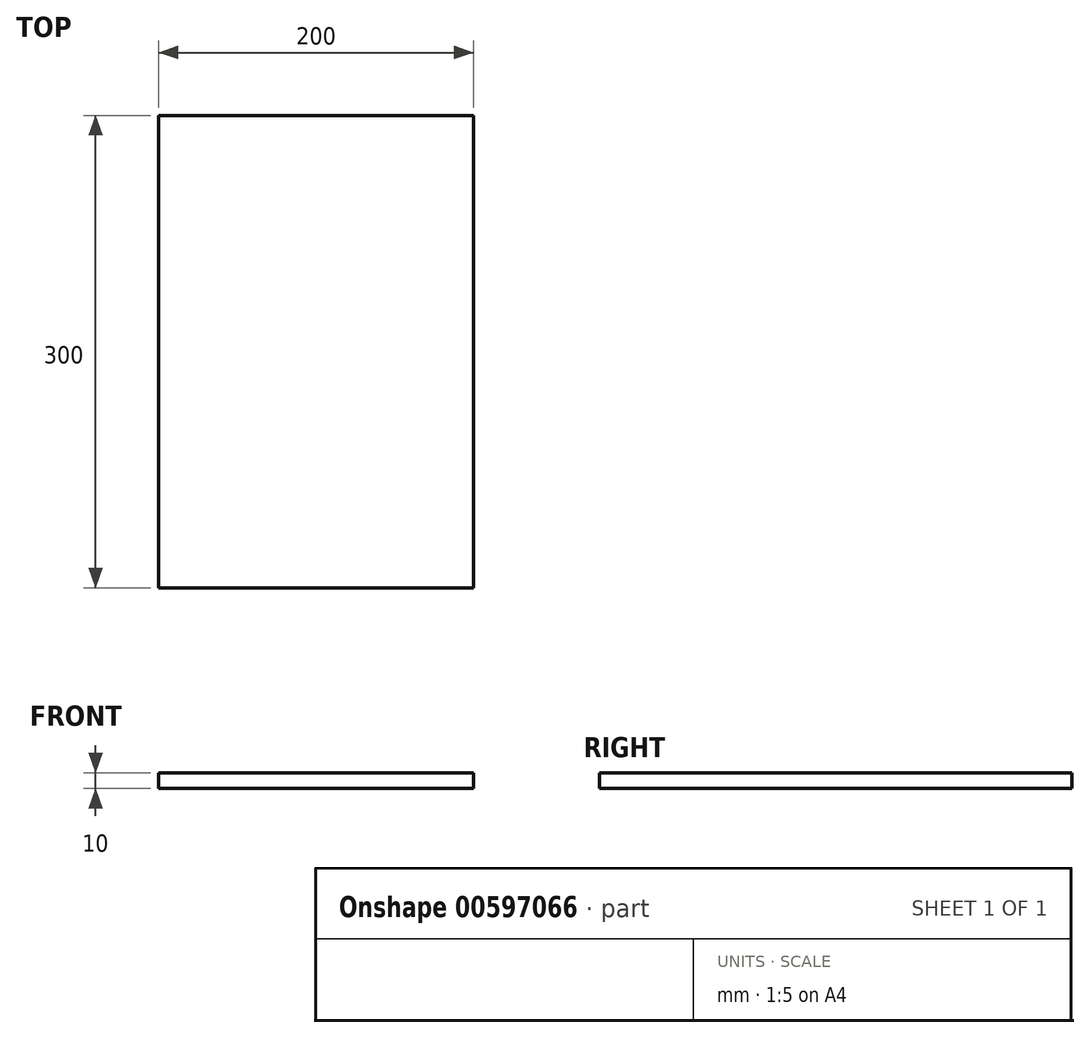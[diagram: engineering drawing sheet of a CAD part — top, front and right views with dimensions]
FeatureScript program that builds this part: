
annotation { "Feature Type Name" : "Feature", "Feature Type Description" : "" }
export const myFeature = defineFeature(function(context is Context, id is Id, definition is map)
    precondition{}
    {
        {
            var Q0;
            Q0=qCreatedBy(makeId("Top.planeOp"),FACE);
            var sketch = newSketch(context, id + "F0", { "sketchPlane" : qUnion([Q0])});
            skLineSegment(sketch, "E0.bottom", {"start": v(0, 0) * mm, "end": v(200, 0) * mm});
            skLineSegment(sketch, "E0.top", {"start": v(0, 300) * mm, "end": v(200, 300) * mm});
            skLineSegment(sketch, "E0.left", {"start": v(0, 0) * mm, "end": v(0, 300) * mm});
            skLineSegment(sketch, "E0.right", {"start": v(200, 0) * mm, "end": v(200, 300) * mm});
            skSolve(sketch);
        }
        {
            var Q0;
            Q0 = qSketchRegion(id + "F0", true);
            extrude(context, id + "F1", {"entities" : qUnion([Q0]), "depth" : 10 * mm, "offsetDistance" : 25 * mm});
        }
    });
